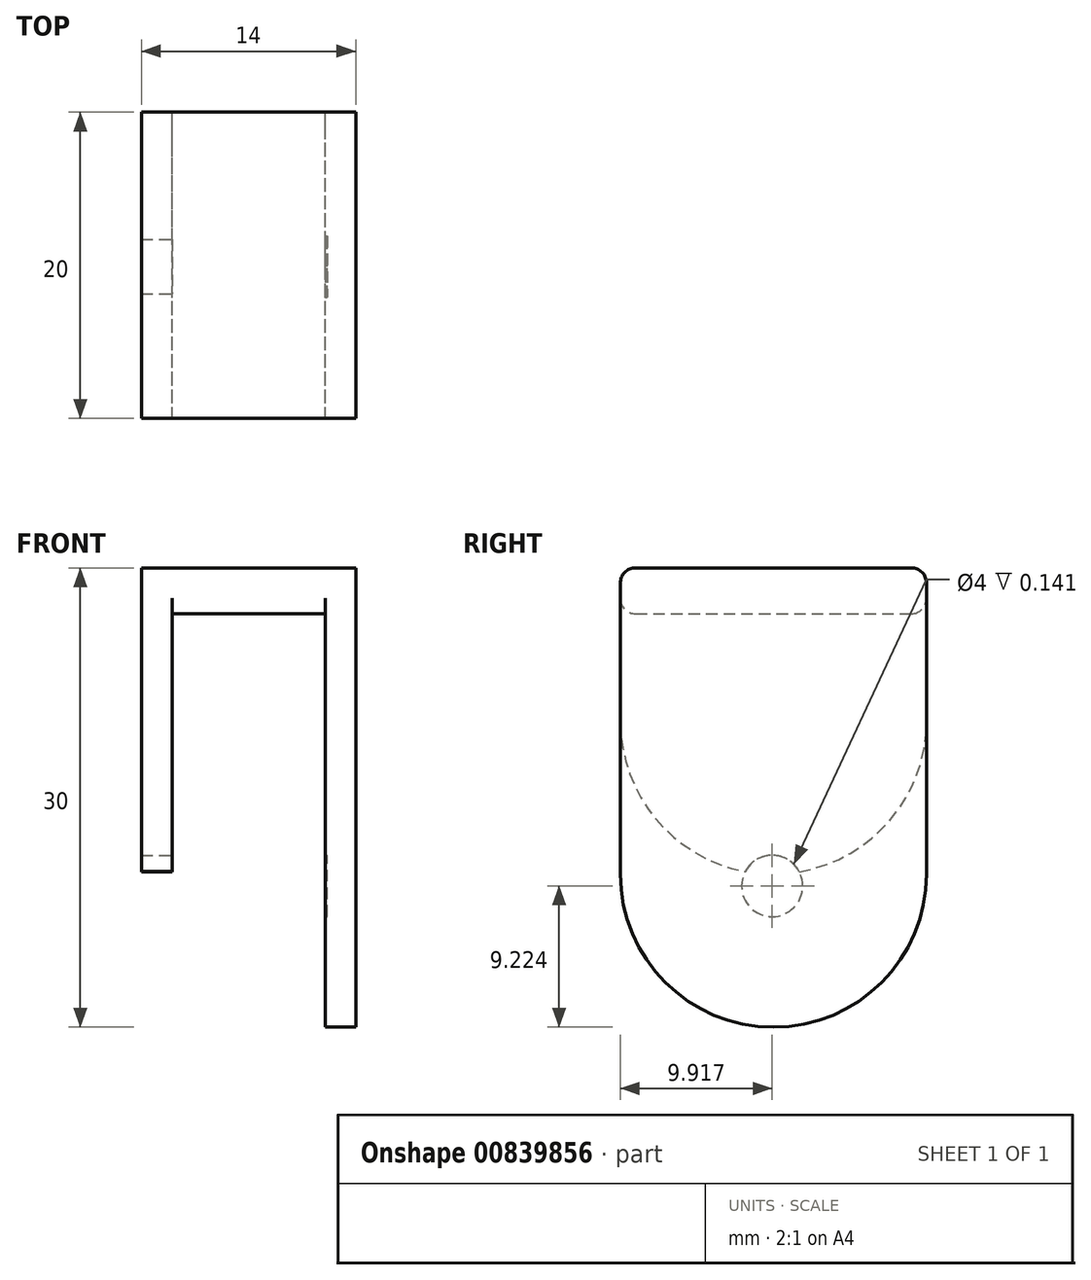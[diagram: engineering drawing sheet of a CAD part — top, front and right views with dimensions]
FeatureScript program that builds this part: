
annotation { "Feature Type Name" : "Feature", "Feature Type Description" : "" }
export const myFeature = defineFeature(function(context is Context, id is Id, definition is map)
    precondition{}
    {
        {
            var Q0;
            Q0=qCreatedBy(makeId("Front.planeOp"),FACE);
            var sketch = newSketch(context, id + "F0", { "sketchPlane" : qUnion([Q0])});
            skLineSegment(sketch, "E0.bottom", {"start": v(-10.14, 3) * mm, "end": v(-0.14, 3) * mm});
            skLineSegment(sketch, "E0.top", {"start": v(-10.14, 0) * mm, "end": v(-0.14, 0) * mm});
            skLineSegment(sketch, "E0.left", {"start": v(-10.14, 3) * mm, "end": v(-10.14, 0) * mm});
            skLineSegment(sketch, "E0.right", {"start": v(-0.14, 3) * mm, "end": v(-0.14, 0) * mm});
            skLineSegment(sketch, "E1.bottom", {"start": v(-10.14, 3) * mm, "end": v(-12.14, 3) * mm});
            skLineSegment(sketch, "E1.top", {"start": v(-10.14, -17) * mm, "end": v(-12.14, -17) * mm});
            skLineSegment(sketch, "E1.left", {"start": v(-10.14, 3) * mm, "end": v(-10.14, -17) * mm});
            skLineSegment(sketch, "E1.right", {"start": v(-12.14, 3) * mm, "end": v(-12.14, -17) * mm});
            skLineSegment(sketch, "E2.bottom", {"start": v(-0.14, 3) * mm, "end": v(1.86, 3) * mm});
            skLineSegment(sketch, "E2.top", {"start": v(-0.14, -27) * mm, "end": v(1.86, -27) * mm});
            skLineSegment(sketch, "E2.left", {"start": v(-0.14, 3) * mm, "end": v(-0.14, -27) * mm});
            skLineSegment(sketch, "E2.right", {"start": v(1.86, 3) * mm, "end": v(1.86, -27) * mm});
            skSolve(sketch);
        }
        {
            var Q0;
            Q0 = qSketchRegion(id + "F0", true);
            extrude(context, id + "F1", {"entities" : qUnion([Q0]), "depth" : 20 * mm, "offsetDistance" : 25 * mm});
        }
        {
            var Q0;
            Q0=makeQuery(id+"F1.opExtrude","CAP_EDGE",EDGE,{"disambiguationData":[OSD([sQuery(id+"F0.wireOp",EDGE,"E1.top")])],"isStart":true});
            var Q1;
            Q1=makeQuery(id+"F1.opExtrude","CAP_EDGE",EDGE,{"disambiguationData":[OSD([sQuery(id+"F0.wireOp",EDGE,"E1.top")])],"isStart":false});
            var Q2;
            Q2=makeQuery(id+"F1.opExtrude","CAP_EDGE",EDGE,{"disambiguationData":[OSD([sQuery(id+"F0.wireOp",EDGE,"E2.top")])],"isStart":false});
            var Q3;
            Q3=makeQuery(id+"F1.opExtrude","CAP_EDGE",EDGE,{"disambiguationData":[OSD([sQuery(id+"F0.wireOp",EDGE,"E2.top")])],"isStart":true});
            fillet(context, id + "F2", {"entities" : qUnion([Q0, Q1, Q2, Q3]), "radius" : 10 * mm, "tangentPropagation" : true, "allowEdgeOverflow" : false});
        }
        {
            var Q0;
            Q0=qCreatedBy(makeId("Right.planeOp"),FACE);
            var sketch = newSketch(context, id + "F3", { "sketchPlane" : qUnion([Q0])});
            skLineSegment(sketch, "E3", {"start": v(-10.08, -17.78) * mm, "end": v(-17.77, -17.78) * mm});
            skSolve(sketch);
        }
        {
            var Q0;
            Q0=sQuery(id+"F3.wireOp",VERTEX,"E3.start");
            var Q1;
            Q1=makeQuery(id+"F1.opExtrude","SWEPT_BODY",BODY,{"disambiguationData":[OSD([sQuery(id+"F0.wireOp",EDGE,"E0.bottom"),sQuery(id+"F0.wireOp",EDGE,"E0.top"),sQuery(id+"F0.wireOp",EDGE,"E1.bottom"),sQuery(id+"F0.wireOp",EDGE,"E1.top"),sQuery(id+"F0.wireOp",EDGE,"E1.left"),sQuery(id+"F0.wireOp",EDGE,"E1.right"),sQuery(id+"F0.wireOp",EDGE,"E2.bottom"),sQuery(id+"F0.wireOp",EDGE,"E2.top"),sQuery(id+"F0.wireOp",EDGE,"E2.left"),sQuery(id+"F0.wireOp",EDGE,"E2.right")])]});
            hole(context, id + "F4", {"style" : HoleStyle.SIMPLE, "endStyle" : HoleEndStyle.THROUGH, "holeDiameter" : 4 * mm, "majorDiameter" : 5 * mm, "isTappedThrough" : true, "tappedDepth" : 12 * mm, "tapClearance" : 3, "locations" : qUnion([Q0]), "scope" : qUnion([Q1])});
        }
        {
            var Q0;
            Q0=makeQuery(id+"F1.opExtrude","CAP_EDGE",EDGE,{"disambiguationData":[OSD([sQuery(id+"F0.wireOp",EDGE,"E0.top")])],"isStart":true});
            var Q1;
            Q1=makeQuery(id+"F1.opExtrude","CAP_EDGE",EDGE,{"disambiguationData":[OSD([sQuery(id+"F0.wireOp",EDGE,"E0.top")])],"isStart":false});
            var Q2;
            Q2=makeQuery(id+"F1.opExtrude","CAP_EDGE",EDGE,{"disambiguationData":[OSD([sQuery(id+"F0.wireOp",EDGE,"E0.bottom"),sQuery(id+"F0.wireOp",EDGE,"E1.bottom"),sQuery(id+"F0.wireOp",EDGE,"E2.bottom")])],"isStart":false});
            var Q3;
            Q3=makeQuery(id+"F1.opExtrude","CAP_EDGE",EDGE,{"disambiguationData":[OSD([sQuery(id+"F0.wireOp",EDGE,"E0.bottom"),sQuery(id+"F0.wireOp",EDGE,"E1.bottom"),sQuery(id+"F0.wireOp",EDGE,"E2.bottom")])],"isStart":true});
            fillet(context, id + "F5", {"entities" : qUnion([Q0, Q1, Q2, Q3]), "radius" : 1 * mm, "tangentPropagation" : true, "allowEdgeOverflow" : false});
        }
    });
